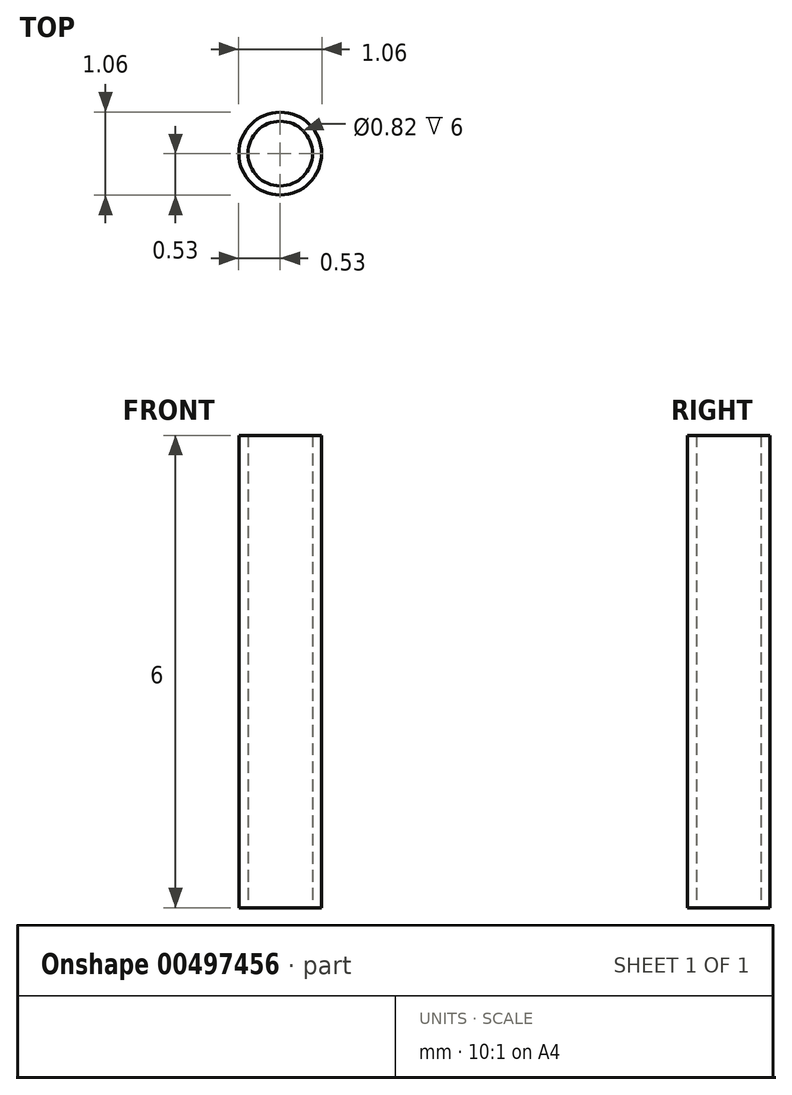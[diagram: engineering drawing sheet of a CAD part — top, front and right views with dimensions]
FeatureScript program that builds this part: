
annotation { "Feature Type Name" : "Feature", "Feature Type Description" : "" }
export const myFeature = defineFeature(function(context is Context, id is Id, definition is map)
    precondition{}
    {
        {
            var Q0;
            Q0=qCreatedBy(makeId("Top.planeOp"),FACE);
            var sketch = newSketch(context, id + "F0", { "sketchPlane" : qUnion([Q0])});
            skCircle(sketch, "E0", {"center": v(0, 0) * mm, "radius": 0.41 * mm});
            skCircle(sketch, "E1", {"center": v(0, 0) * mm, "radius": 0.53 * mm});
            skSolve(sketch);
        }
        {
            var Q0;
            Q0=makeQuery(id+"F0.imprint","IMPRINT",FACE,{"disambiguationData":[TD([[makeQuery(id+"F0.imprint","IMPRINT",EDGE,{"derivedFrom":sQuery(id+"F0.wireOp",EDGE,"E0")}),-1.0]])]});
            extrude(context, id + "F1", {"entities" : qUnion([Q0]), "depth" : 6 * mm});
        }
    });
